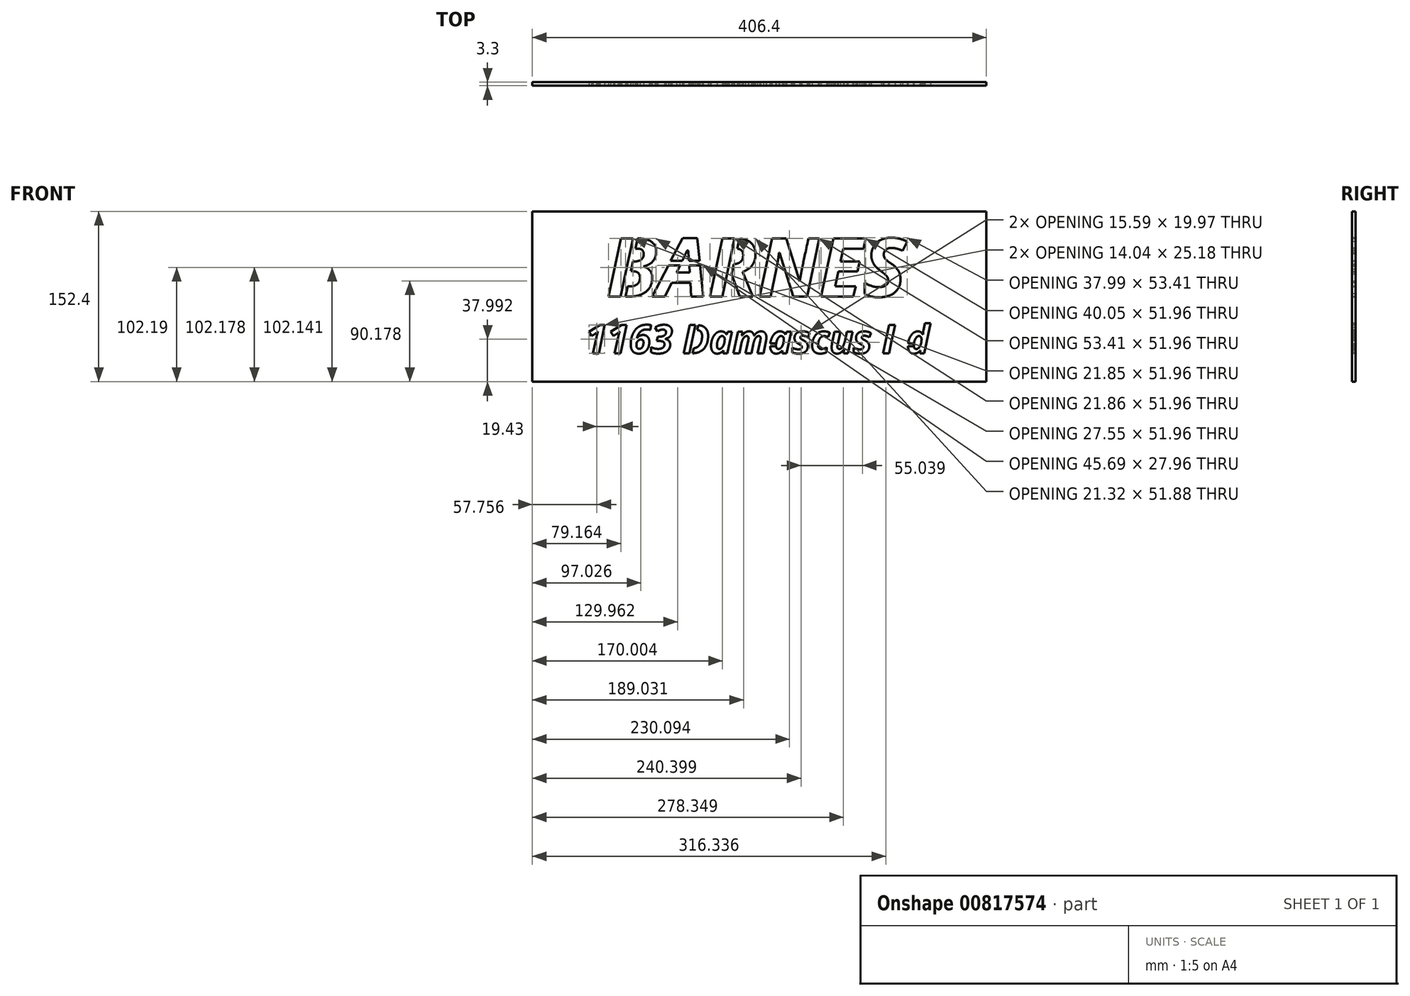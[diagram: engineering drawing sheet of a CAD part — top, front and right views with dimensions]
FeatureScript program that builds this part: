
annotation { "Feature Type Name" : "Feature", "Feature Type Description" : "" }
export const myFeature = defineFeature(function(context is Context, id is Id, definition is map)
    precondition{}
    {
        {
            var Q0;
            Q0=qCreatedBy(makeId("Front.planeOp"),FACE);
            var sketch = newSketch(context, id + "F0", { "sketchPlane" : qUnion([Q0])});
            skLineSegment(sketch, "E0.bottom", {"start": v(-203.2, 76.2) * mm, "end": v(203.2, 76.2) * mm});
            skLineSegment(sketch, "E0.top", {"start": v(-203.2, -76.2) * mm, "end": v(203.2, -76.2) * mm});
            skLineSegment(sketch, "E0.left", {"start": v(-203.2, 76.2) * mm, "end": v(-203.2, -76.2) * mm});
            skLineSegment(sketch, "E0.right", {"start": v(203.2, 76.2) * mm, "end": v(203.2, -76.2) * mm});
            skPoint(sketch, "E0.middle", {"position": v(0, 0) * mm});
            skSolve(sketch);
        }
        {
            var Q0;
            Q0=makeQuery(id+"F0.imprint","IMPRINT",FACE,{"disambiguationData":[TD([[makeQuery(id+"F0.imprint","IMPRINT",EDGE,{"derivedFrom":sQuery(id+"F0.wireOp",EDGE,"E0.bottom")}),-1.0]])]});
            extrude(context, id + "F1", {"entities" : qUnion([Q0]), "depth" : 3.3 * mm, "offsetDistance" : 25.4 * mm});
        }
        {
            var Q0;
            Q0=makeQuery(id+"F1.opExtrude","CAP_FACE",FACE,{"disambiguationData":[OSD([sQuery(id+"F0.wireOp",EDGE,"E0.bottom"),sQuery(id+"F0.wireOp",EDGE,"E0.top"),sQuery(id+"F0.wireOp",EDGE,"E0.left"),sQuery(id+"F0.wireOp",EDGE,"E0.right")])],"isStart":false});
            var sketch = newSketch(context, id + "F2", { "sketchPlane" : qUnion([Q0])});
            skText(sketch, "E1", { "text": "BARNES", "fontName": "OpenSans-BoldItalic.ttf"});
            const initialGuessF2  = {"E1": [-0.13685, 0, 1, 0, 0.0524]};
            skSetInitialGuess(sketch, initialGuessF2);
            skSolve(sketch);
        }
        {
            var Q0;
            Q0 = qSketchRegion(id + "F2", true);
            extrude(context, id + "F3", {"entities" : qUnion([Q0]), "operationType" : NewBodyOperationType.REMOVE, "oppositeDirection" : true, "depth" : 25.4 * mm, "offsetDistance" : 25.4 * mm});
        }
        {
            var Q0;
            {var subQ0=sQuery(id+"F0.wireOp",EDGE,"E0.left");var subQ1=sQuery(id+"F0.wireOp",EDGE,"E0.bottom");var subQ2=sQuery(id+"F0.wireOp",EDGE,"E0.right");var subQ3=sQuery(id+"F0.wireOp",EDGE,"E0.top");Q0=makeQuery(id+"F3.boolean.opBoolean","SPLIT",FACE,{"disambiguationData":[TD([makeQuery(id+"F1.opExtrude","SWEPT_FACE",FACE,{"disambiguationData":[OSD([subQ1])]})])],"derivedFrom":makeQuery(id+"F1.opExtrude","CAP_FACE",FACE,{"disambiguationData":[OSD([subQ1,subQ3,subQ0,subQ2])],"isStart":false})});}
            var sketch = newSketch(context, id + "F4", { "sketchPlane" : qUnion([Q0])});
            skLineSegment(sketch, "E2", {"start": v(-119.95, 0) * mm, "end": v(-108.9, 51.96) * mm});
            skLineSegment(sketch, "E3", {"start": v(-124.16, 0) * mm, "end": v(-113.1, 51.96) * mm});
            skLineSegment(sketch, "E4", {"start": v(-113.1, 51.96) * mm, "end": v(-108.9, 51.96) * mm});
            skLineSegment(sketch, "E5", {"start": v(-124.16, 0) * mm, "end": v(-119.95, 0) * mm});
            skLineSegment(sketch, "E6", {"start": v(-29.06, 19.93) * mm, "end": v(-22.26, 51.96) * mm});
            skLineSegment(sketch, "E7", {"start": v(-24.83, 19.93) * mm, "end": v(-18.05, 51.88) * mm});
            skLineSegment(sketch, "E8", {"start": v(-29.06, 19.93) * mm, "end": v(-24.83, 19.93) * mm});
            skLineSegment(sketch, "E9.0", {"start": v(-22.26, 51.96) * mm, "end": v(-20.4, 51.96) * mm});
            skFitSpline(sketch, "E10.0", {"points": [v(-20.29, 51.69) * mm, v(-11.9, 51.69) * mm, v(-7.7, 48.08) * mm]});
            skPoint(sketch, "E11.orphan", {"position": v(-33.15, 51.96) * mm});
            skPoint(sketch, "E12.orphan", {"position": v(-7.74, 48.33) * mm});
            skLineSegment(sketch, "E13", {"start": v(-79.36, 32.07) * mm, "end": v(-53.6, 32.07) * mm});
            skLineSegment(sketch, "E14", {"start": v(-53.6, 32.07) * mm, "end": v(-53.19, 27.96) * mm});
            skLineSegment(sketch, "E15", {"start": v(-53.19, 27.96) * mm, "end": v(-81.5, 27.96) * mm});
            skLineSegment(sketch, "E16", {"start": v(-81.5, 27.96) * mm, "end": v(-79.36, 32.07) * mm});
            skSolve(sketch);
        }
        {
            var Q0;
            Q0=makeQuery(id+"F4.imprint","IMPRINT",FACE,{"disambiguationData":[TD([[makeQuery(id+"F4.imprint","IMPRINT",EDGE,{"derivedFrom":sQuery(id+"F4.wireOp",EDGE,"E2")}),1.0]])]});
            var Q1;
            Q1=makeQuery(id+"F4.imprint","IMPRINT",FACE,{"disambiguationData":[TD([[makeQuery(id+"F4.imprint","IMPRINT",EDGE,{"derivedFrom":sQuery(id+"F4.wireOp",EDGE,"E6")}),-1.0]])]});
            var Q2;
            Q2=makeQuery(id+"F4.imprint","IMPRINT",FACE,{"disambiguationData":[TD([[makeQuery(id+"F4.imprint","IMPRINT",EDGE,{"derivedFrom":sQuery(id+"F4.wireOp",EDGE,"76jXHiS7-TY4x-8zlB-wRIJ-2QAKeQL3fKV6")}),-1.0]])]});
            var Q3;
            Q3=makeQuery(id+"F4.imprint","IMPRINT",FACE,{"disambiguationData":[TD([[makeQuery(id+"F4.imprint","IMPRINT",EDGE,{"derivedFrom":sQuery(id+"F4.wireOp",EDGE,"E13")}),-1.0]])]});
            var Q4;
            {var subQ0=sQuery(id+"F0.wireOp",EDGE,"E0.left");var subQ1=sQuery(id+"F0.wireOp",EDGE,"E0.bottom");var subQ2=sQuery(id+"F0.wireOp",EDGE,"E0.right");var subQ3=sQuery(id+"F0.wireOp",EDGE,"E0.top");Q4=makeQuery(id+"F3.boolean.opBoolean","SPLIT",FACE,{"disambiguationData":[TD([makeQuery(id+"F1.opExtrude","SWEPT_FACE",FACE,{"disambiguationData":[OSD([subQ1])]})])],"derivedFrom":makeQuery(id+"F1.opExtrude","CAP_FACE",FACE,{"disambiguationData":[OSD([subQ1,subQ3,subQ0,subQ2])],"isStart":true})});}
            extrude(context, id + "F5", {"entities" : qUnion([Q0, Q1, Q2, Q3]), "operationType" : NewBodyOperationType.ADD, "endBound" : BoundingType.UP_TO_SURFACE, "oppositeDirection" : true, "depth" : 25.4 * mm, "endBoundEntityFace" : qUnion([Q4]), "offsetDistance" : 25.4 * mm});
        }
        {
            var Q0;
            Q0=makeQuery(id+"F3.boolean.opBoolean","COPY",EDGE,{"derivedFrom":makeQuery(id+"F3.opExtrude","SWEPT_EDGE",EDGE,{"disambiguationData":[OSD([sQuery(id+"F2.wireOp",EDGE,"E1.sketch_text.stroke-34"),sQuery(id+"F2.wireOp",EDGE,"E1.sketch_text.stroke-35")])]})});
            fillet(context, id + "F6", {"entities" : qUnion([Q0]), "radius" : 0.76 * mm, "tangentPropagation" : true, "allowEdgeOverflow" : false});
        }
        {
            var Q0;
            {var subQ0=sQuery(id+"F0.wireOp",EDGE,"E0.right");var subQ1=sQuery(id+"F0.wireOp",EDGE,"E0.left");var subQ2=sQuery(id+"F0.wireOp",EDGE,"E0.top");var subQ3=sQuery(id+"F0.wireOp",EDGE,"E0.bottom");var subQ4=makeQuery(id+"F1.opExtrude","CAP_FACE",FACE,{"disambiguationData":[OSD([subQ3,subQ2,subQ1,subQ0])],"isStart":false});Q0=makeQuery(id+"F5.boolean.opBoolean","MERGE",FACE,{"derivedFrom":[makeQuery(id+"F3.boolean.opBoolean","SPLIT",FACE,{"disambiguationData":[TD([makeQuery(id+"F1.opExtrude","SWEPT_FACE",FACE,{"disambiguationData":[OSD([subQ3])]})])],"derivedFrom":subQ4}),makeQuery(id+"F3.boolean.opBoolean","SPLIT",FACE,{"disambiguationData":[TD([makeQuery(id+"F3.opExtrude","SWEPT_FACE",FACE,{"disambiguationData":[OSD([sQuery(id+"F2.wireOp",EDGE,"E1.sketch_text.stroke-12")])]})])],"derivedFrom":subQ4}),makeQuery(id+"F3.boolean.opBoolean","SPLIT",FACE,{"disambiguationData":[TD([makeQuery(id+"F3.opExtrude","SWEPT_FACE",FACE,{"disambiguationData":[OSD([sQuery(id+"F2.wireOp",EDGE,"E1.sketch_text.stroke-18")])]})])],"derivedFrom":subQ4}),makeQuery(id+"F3.boolean.opBoolean","SPLIT",FACE,{"disambiguationData":[TD([makeQuery(id+"F3.opExtrude","SWEPT_FACE",FACE,{"disambiguationData":[OSD([sQuery(id+"F2.wireOp",EDGE,"E1.sketch_text.stroke-32")])]})])],"derivedFrom":subQ4}),makeQuery(id+"F3.boolean.opBoolean","SPLIT",FACE,{"disambiguationData":[TD([makeQuery(id+"F3.opExtrude","SWEPT_FACE",FACE,{"disambiguationData":[OSD([sQuery(id+"F2.wireOp",EDGE,"E1.sketch_text.stroke-38")])]})])],"derivedFrom":subQ4}),makeQuery(id+"F5.opExtrude","CAP_FACE",FACE,{"disambiguationData":[OSD([sQuery(id+"F4.wireOp",EDGE,"E2"),sQuery(id+"F4.wireOp",EDGE,"E3"),sQuery(id+"F4.wireOp",EDGE,"E4"),sQuery(id+"F4.wireOp",EDGE,"E5")])],"isStart":true}),makeQuery(id+"F5.opExtrude","CAP_FACE",FACE,{"disambiguationData":[OSD([sQuery(id+"F4.wireOp",EDGE,"E6"),sQuery(id+"F4.wireOp",EDGE,"E7"),sQuery(id+"F4.wireOp",EDGE,"E8"),sQuery(id+"F4.wireOp",EDGE,"E9.0"),sQuery(id+"F4.wireOp",EDGE,"E10.0")])],"isStart":true}),makeQuery(id+"F5.opExtrude","CAP_FACE",FACE,{"disambiguationData":[OSD([sQuery(id+"F4.wireOp",EDGE,"E13"),sQuery(id+"F4.wireOp",EDGE,"E14"),sQuery(id+"F4.wireOp",EDGE,"E15"),sQuery(id+"F4.wireOp",EDGE,"E16")])],"isStart":true})]});}
            var sketch = newSketch(context, id + "F7", { "sketchPlane" : qUnion([Q0])});
            skText(sketch, "E17", { "text": "1163 Damascus Rd", "fontName": "OpenSans-BoldItalic.ttf"});
            const initialGuessF7  = {"E17": [-0.1556, -0.0508, 1, 0, 0.0254]};
            skSetInitialGuess(sketch, initialGuessF7);
            skSolve(sketch);
        }
        {
            var Q0;
            Q0 = qSketchRegion(id + "F7", true);
            extrude(context, id + "F8", {"entities" : qUnion([Q0]), "operationType" : NewBodyOperationType.REMOVE, "oppositeDirection" : true, "depth" : 25.4 * mm, "offsetDistance" : 25.4 * mm});
        }
        {
            var Q0;
            {var subQ0=sQuery(id+"F4.wireOp",EDGE,"E7");var subQ18=sQuery(id+"F4.wireOp",EDGE,"E13");var subQ20=makeQuery(id+"F3.opExtrude","SWEPT_FACE",FACE,{"disambiguationData":[OSD([sQuery(id+"F2.wireOp",EDGE,"E1.sketch_text.stroke-38")])]});var subQ26=sQuery(id+"F4.wireOp",EDGE,"E6");var subQ28=makeQuery(id+"F3.opExtrude","SWEPT_FACE",FACE,{"disambiguationData":[OSD([sQuery(id+"F2.wireOp",EDGE,"E1.sketch_text.stroke-32")])]});var subQ31=sQuery(id+"F4.wireOp",EDGE,"E3");var subQ35=sQuery(id+"F4.wireOp",EDGE,"E2");var subQ45=makeQuery(id+"F3.opExtrude","SWEPT_FACE",FACE,{"disambiguationData":[OSD([sQuery(id+"F2.wireOp",EDGE,"E1.sketch_text.stroke-18")])]});var subQ51=sQuery(id+"F4.wireOp",EDGE,"E15");var subQ54=sQuery(id+"F0.wireOp",EDGE,"E0.bottom");var subQ55=makeQuery(id+"F1.opExtrude","SWEPT_FACE",FACE,{"disambiguationData":[OSD([subQ54])]});var subQ60=sQuery(id+"F0.wireOp",EDGE,"E0.right");var subQ65=sQuery(id+"F0.wireOp",EDGE,"E0.top");var subQ69=sQuery(id+"F0.wireOp",EDGE,"E0.left");var subQ79=makeQuery(id+"F3.opExtrude","SWEPT_FACE",FACE,{"disambiguationData":[OSD([sQuery(id+"F2.wireOp",EDGE,"E1.sketch_text.stroke-12")])]});var subQ121=makeQuery(id+"F1.opExtrude","CAP_FACE",FACE,{"disambiguationData":[OSD([subQ54,subQ65,subQ69,subQ60])],"isStart":false});Q0=makeQuery(id+"F8.boolean.opBoolean","SPLIT",FACE,{"disambiguationData":[TD([subQ55])],"derivedFrom":makeQuery(id+"F5.boolean.opBoolean","MERGE",FACE,{"derivedFrom":[makeQuery(id+"F3.boolean.opBoolean","SPLIT",FACE,{"disambiguationData":[TD([subQ55])],"derivedFrom":subQ121}),makeQuery(id+"F3.boolean.opBoolean","SPLIT",FACE,{"disambiguationData":[TD([subQ79])],"derivedFrom":subQ121}),makeQuery(id+"F3.boolean.opBoolean","SPLIT",FACE,{"disambiguationData":[TD([subQ45])],"derivedFrom":subQ121}),makeQuery(id+"F3.boolean.opBoolean","SPLIT",FACE,{"disambiguationData":[TD([subQ28])],"derivedFrom":subQ121}),makeQuery(id+"F3.boolean.opBoolean","SPLIT",FACE,{"disambiguationData":[TD([subQ20])],"derivedFrom":subQ121}),makeQuery(id+"F5.opExtrude","CAP_FACE",FACE,{"disambiguationData":[OSD([subQ35,subQ31,sQuery(id+"F4.wireOp",EDGE,"E4"),sQuery(id+"F4.wireOp",EDGE,"E5")])],"isStart":true}),makeQuery(id+"F5.opExtrude","CAP_FACE",FACE,{"disambiguationData":[OSD([subQ26,subQ0,sQuery(id+"F4.wireOp",EDGE,"E8"),sQuery(id+"F4.wireOp",EDGE,"E9.0"),sQuery(id+"F4.wireOp",EDGE,"E10.0")])],"isStart":true}),makeQuery(id+"F5.opExtrude","CAP_FACE",FACE,{"disambiguationData":[OSD([subQ18,sQuery(id+"F4.wireOp",EDGE,"E14"),subQ51,sQuery(id+"F4.wireOp",EDGE,"E16")])],"isStart":true})]})});}
            var sketch = newSketch(context, id + "F9", { "sketchPlane" : qUnion([Q0])});
            skLineSegment(sketch, "E18", {"start": v(-115.22, -41.91) * mm, "end": v(-103.78, -41.91) * mm});
            skLineSegment(sketch, "E19", {"start": v(-115.14, -44.45) * mm, "end": v(-104.38, -44.45) * mm});
            skFitSpline(sketch, "E20.0", {"points": [v(-113.37, -48.96) * mm, v(-115.23, -46.77) * mm, v(-115.23, -42.72) * mm]});
            skFitSpline(sketch, "E21.0", {"points": [v(-115.23, -42.72) * mm, v(-115.23, -39.24) * mm, v(-114.18, -35.9) * mm]});
            skLineSegment(sketch, "E22", {"start": v(-57.21, -25.61) * mm, "end": v(-62.56, -50.8) * mm});
            skLineSegment(sketch, "E23", {"start": v(-62.56, -50.8) * mm, "end": v(-59.96, -50.8) * mm});
            skLineSegment(sketch, "E24", {"start": v(-59.96, -50.8) * mm, "end": v(-54.62, -25.61) * mm});
            skLineSegment(sketch, "E25", {"start": v(-54.62, -25.61) * mm, "end": v(-57.21, -25.61) * mm});
            skLineSegment(sketch, "E26", {"start": v(-32.54, -44.45) * mm, "end": v(-43.3, -44.45) * mm});
            skLineSegment(sketch, "E27", {"start": v(-43.16, -41.91) * mm, "end": v(-31.52, -41.91) * mm});
            skFitSpline(sketch, "E28.0", {"points": [v(-33.53, -45.8) * mm, v(-32.43, -44.65) * mm, v(-31.76, -42.68) * mm]});
            skFitSpline(sketch, "E29.0", {"points": [v(-31.76, -42.68) * mm, v(-31.08, -40.7) * mm, v(-31.08, -38.21) * mm]});
            skPoint(sketch, "E30.orphan", {"position": v(-31.08, -38.21) * mm});
            skPoint(sketch, "E31.orphan", {"position": v(-33.53, -45.8) * mm});
            skFitSpline(sketch, "E32.0", {"points": [v(-104.84, -45.27) * mm, v(-103.76, -43.65) * mm, v(-103.76, -41.2) * mm]});
            skPoint(sketch, "E33.orphan", {"position": v(-103.76, -41.2) * mm});
            skPoint(sketch, "E34.orphan", {"position": v(-104.84, -45.27) * mm});
            skFitSpline(sketch, "E35.0", {"points": [v(-41.84, -49.31) * mm, v(-43.3, -47.48) * mm, v(-43.3, -44.17) * mm]});
            skFitSpline(sketch, "E36.0", {"points": [v(-43.3, -44.17) * mm, v(-43.3, -40.76) * mm, v(-42.06, -37.66) * mm]});
            skPoint(sketch, "E37.orphan", {"position": v(-42.06, -37.66) * mm});
            skPoint(sketch, "E38.orphan", {"position": v(-41.84, -49.31) * mm});
            skLineSegment(sketch, "E39", {"start": v(9.73, -41.91) * mm, "end": v(15, -41.91) * mm});
            skLineSegment(sketch, "E40", {"start": v(9.59, -44.45) * mm, "end": v(14.86, -44.45) * mm});
            skFitSpline(sketch, "E41.0", {"points": [v(11.04, -49.31) * mm, v(9.59, -47.48) * mm, v(9.59, -44.17) * mm]});
            skFitSpline(sketch, "E42.0", {"points": [v(9.59, -44.17) * mm, v(9.59, -40.76) * mm, v(10.83, -37.66) * mm]});
            skFitSpline(sketch, "E43.0", {"points": [v(15.47, -39.9) * mm, v(14.84, -41.93) * mm, v(14.84, -43.93) * mm]});
            skFitSpline(sketch, "E44.0", {"points": [v(14.84, -43.93) * mm, v(14.84, -45.44) * mm, v(15.42, -46.2) * mm]});
            skPoint(sketch, "E45.orphan", {"position": v(10.83, -37.66) * mm});
            skPoint(sketch, "E46.orphan", {"position": v(11.04, -49.31) * mm});
            skPoint(sketch, "E47.orphan", {"position": v(15.42, -46.2) * mm});
            skPoint(sketch, "E48.orphan", {"position": v(15.47, -39.9) * mm});
            skLineSegment(sketch, "E49", {"start": v(118.11, -41.14) * mm, "end": v(121.4, -25.61) * mm});
            skLineSegment(sketch, "E50", {"start": v(120.16, -41.14) * mm, "end": v(123.45, -25.65) * mm});
            skLineSegment(sketch, "E51.0", {"start": v(121.4, -25.61) * mm, "end": v(122.31, -25.61) * mm});
            skFitSpline(sketch, "E52.0", {"points": [v(122.31, -25.61) * mm, v(126.4, -25.61) * mm, v(128.45, -27.37) * mm]});
            skPoint(sketch, "E53.orphan", {"position": v(116.13, -25.61) * mm});
            skPoint(sketch, "E54.orphan", {"position": v(128.45, -27.37) * mm});
            skLineSegment(sketch, "E55", {"start": v(118.11, -41.14) * mm, "end": v(120.16, -41.14) * mm});
            skLineSegment(sketch, "E56", {"start": v(133.06, -41.91) * mm, "end": v(138.34, -41.91) * mm});
            skLineSegment(sketch, "E57", {"start": v(132.93, -44.45) * mm, "end": v(138.2, -44.45) * mm});
            skFitSpline(sketch, "E58.0", {"points": [v(132.93, -44.14) * mm, v(132.93, -40.76) * mm, v(134.16, -37.68) * mm]});
            skFitSpline(sketch, "E59.0", {"points": [v(134.38, -49.3) * mm, v(132.93, -47.46) * mm, v(132.93, -44.14) * mm]});
            skFitSpline(sketch, "E60.0", {"points": [v(138.18, -43.93) * mm, v(138.18, -46.96) * mm, v(140.54, -46.96) * mm]});
            skFitSpline(sketch, "E61.0", {"points": [v(138.8, -39.9) * mm, v(138.18, -41.93) * mm, v(138.18, -43.93) * mm]});
            skPoint(sketch, "E62.orphan", {"position": v(134.16, -37.68) * mm});
            skPoint(sketch, "E63.orphan", {"position": v(134.38, -49.3) * mm});
            skPoint(sketch, "E64.orphan", {"position": v(140.54, -46.96) * mm});
            skPoint(sketch, "E65.orphan", {"position": v(138.8, -39.9) * mm});
            skSolve(sketch);
        }
        {
            var Q0;
            Q0=makeQuery(id+"F9.imprint","IMPRINT",FACE,{"disambiguationData":[TD([[makeQuery(id+"F9.imprint","IMPRINT",EDGE,{"derivedFrom":sQuery(id+"F9.wireOp",EDGE,"E18")}),-1.0]])]});
            var Q1;
            {var subQ7=sQuery(id+"F9.wireOp",EDGE,"E22");Q1=makeQuery(id+"F9.imprint","IMPRINT",FACE,{"disambiguationData":[TD([[makeQuery(id+"F9.imprint","IMPRINT",EDGE,{"derivedFrom":subQ7}),1.0]])]});}
            var Q2;
            Q2=makeQuery(id+"F9.imprint","IMPRINT",FACE,{"disambiguationData":[TD([[makeQuery(id+"F9.imprint","IMPRINT",EDGE,{"derivedFrom":sQuery(id+"F9.wireOp",EDGE,"B6xI3UDl-oJuq-2wAy-hm6m-3ZBFRS7hD8t0")}),-1.0]])]});
            var Q3;
            Q3=makeQuery(id+"F9.imprint","IMPRINT",FACE,{"disambiguationData":[TD([[makeQuery(id+"F9.imprint","IMPRINT",EDGE,{"derivedFrom":sQuery(id+"F9.wireOp",EDGE,"KJzyAJjO-dG91-cgSx-8UrG-amPT9Q8SzFFY")}),-1.0]])]});
            var Q4;
            Q4=makeQuery(id+"F9.imprint","IMPRINT",FACE,{"disambiguationData":[TD([[makeQuery(id+"F9.imprint","IMPRINT",EDGE,{"derivedFrom":sQuery(id+"F9.wireOp",EDGE,"E26")}),-1.0]])]});
            var Q5;
            Q5=makeQuery(id+"F9.imprint","IMPRINT",FACE,{"disambiguationData":[TD([[makeQuery(id+"F9.imprint","IMPRINT",EDGE,{"derivedFrom":sQuery(id+"F9.wireOp",EDGE,"E39")}),-1.0]])]});
            var Q6;
            Q6=makeQuery(id+"F9.imprint","IMPRINT",FACE,{"disambiguationData":[TD([[makeQuery(id+"F9.imprint","IMPRINT",EDGE,{"derivedFrom":sQuery(id+"F9.wireOp",EDGE,"E49")}),-1.0]])]});
            var Q7;
            Q7=makeQuery(id+"F9.imprint","IMPRINT",FACE,{"disambiguationData":[TD([[makeQuery(id+"F9.imprint","IMPRINT",EDGE,{"derivedFrom":sQuery(id+"F9.wireOp",EDGE,"E56")}),-1.0]])]});
            var Q8;
            {var subQ18=makeQuery(id+"F3.opExtrude","SWEPT_FACE",FACE,{"disambiguationData":[OSD([sQuery(id+"F2.wireOp",EDGE,"E1.sketch_text.stroke-38")])]});var subQ25=makeQuery(id+"F3.opExtrude","SWEPT_FACE",FACE,{"disambiguationData":[OSD([sQuery(id+"F2.wireOp",EDGE,"E1.sketch_text.stroke-32")])]});var subQ40=makeQuery(id+"F3.opExtrude","SWEPT_FACE",FACE,{"disambiguationData":[OSD([sQuery(id+"F2.wireOp",EDGE,"E1.sketch_text.stroke-18")])]});var subQ48=sQuery(id+"F0.wireOp",EDGE,"E0.bottom");var subQ49=makeQuery(id+"F1.opExtrude","SWEPT_FACE",FACE,{"disambiguationData":[OSD([subQ48])]});var subQ54=sQuery(id+"F0.wireOp",EDGE,"E0.right");var subQ59=sQuery(id+"F0.wireOp",EDGE,"E0.top");var subQ63=sQuery(id+"F0.wireOp",EDGE,"E0.left");var subQ73=makeQuery(id+"F3.opExtrude","SWEPT_FACE",FACE,{"disambiguationData":[OSD([sQuery(id+"F2.wireOp",EDGE,"E1.sketch_text.stroke-12")])]});var subQ115=makeQuery(id+"F1.opExtrude","CAP_FACE",FACE,{"disambiguationData":[OSD([subQ48,subQ59,subQ63,subQ54])],"isStart":true});Q8=makeQuery(id+"F8.boolean.opBoolean","SPLIT",FACE,{"disambiguationData":[TD([subQ49])],"derivedFrom":makeQuery(id+"F5.boolean.opBoolean","MERGE",FACE,{"derivedFrom":[makeQuery(id+"F3.boolean.opBoolean","SPLIT",FACE,{"disambiguationData":[TD([subQ73])],"derivedFrom":subQ115}),makeQuery(id+"F3.boolean.opBoolean","SPLIT",FACE,{"disambiguationData":[TD([subQ40])],"derivedFrom":subQ115}),makeQuery(id+"F3.boolean.opBoolean","SPLIT",FACE,{"disambiguationData":[TD([subQ25])],"derivedFrom":subQ115}),makeQuery(id+"F3.boolean.opBoolean","SPLIT",FACE,{"disambiguationData":[TD([subQ18])],"derivedFrom":subQ115}),makeQuery(id+"F3.boolean.opBoolean","SPLIT",FACE,{"disambiguationData":[TD([subQ49])],"derivedFrom":subQ115}),makeQuery(id+"F5.opExtrude","CAP_FACE",FACE,{"disambiguationData":[OSD([subQ48,subQ59,subQ63,subQ54]),OD(0.0)],"isStart":false}),makeQuery(id+"F5.opExtrude","CAP_FACE",FACE,{"disambiguationData":[OSD([subQ48,subQ59,subQ63,subQ54]),OD(1.0)],"isStart":false}),makeQuery(id+"F5.opExtrude","CAP_FACE",FACE,{"disambiguationData":[OSD([subQ48,subQ59,subQ63,subQ54]),OD(2.0)],"isStart":false})]})});}
            extrude(context, id + "F10", {"entities" : qUnion([Q0, Q1, Q2, Q3, Q4, Q5, Q6, Q7]), "operationType" : NewBodyOperationType.ADD, "endBound" : BoundingType.UP_TO_SURFACE, "oppositeDirection" : true, "depth" : 25.4 * mm, "endBoundEntityFace" : qUnion([Q8]), "offsetDistance" : 25.4 * mm});
        }
    });
